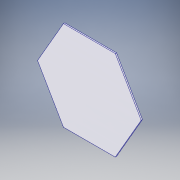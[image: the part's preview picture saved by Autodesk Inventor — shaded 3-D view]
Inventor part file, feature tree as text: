
AUTODESK INVENTOR PART (.ipt)
format: ipt  version: 2019 (Build 230136000, 136)  size: 96,768 bytes
history: native  units: mm
features: extrude x1, sketch x1
ambient origin geometry x8: Origin, YZ Plane, XZ Plane, XY Plane, X Axis, Y Axis, Z Axis, Center Point
bodies: Solid1 (feature_tree)
feature tree (2):
  extrude  "Extrusion1"  Depth=2.0mm TaperAngle=0.0deg
  sketch  "Sketch1"  dims[d0=142.0mm d1=2.0mm d2=0.0mm]
